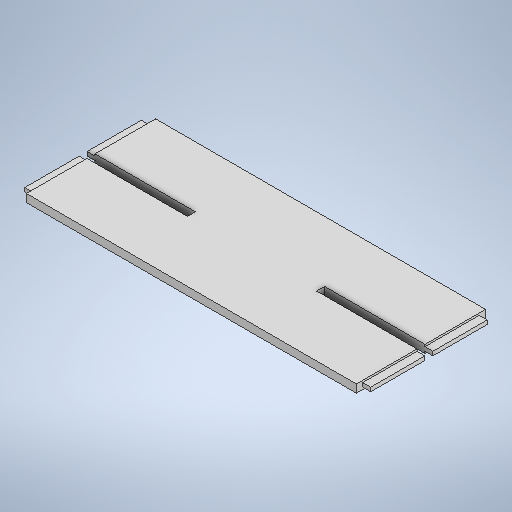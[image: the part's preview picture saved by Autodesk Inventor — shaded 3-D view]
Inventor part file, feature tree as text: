
AUTODESK INVENTOR PART (.ipt)
format: ipt  version: 2025.2 (Build 292293000, 293)  size: 275,456 bytes
history: native  units: mm
features: extrude x3, sketch x3, plane x1, mirror x1
ambient origin geometry x8: Origin, YZ Plane, XZ Plane, XY Plane, X Axis, Y Axis, Z Axis, Center Point
bodies: Solid1 (feature_tree)
feature tree (8):
  extrude  "Extrusion1"  Depth=77.381mm
  extrude  "Extrusion2"  Depth=4.763mm
  extrude  "Extrusion3"  Depth=4.763mm TaperAngle=0.0deg
  plane  "Work Plane1"
  mirror  "Mirror1"
  sketch  "Sketch1"  dims[d0=197.626mm d1=77.381mm]
  sketch  "Sketch2"  dims[d2=4.763mm d3=0.0mm d6=4.763mm]
  sketch  "Sketch3"  dims[d7=60.123mm d8=22.0mm d9=0.0mm d12=32.503mm d13=4.763mm d14=0.0mm]
